# Revit family: Deca_Porta toalha barra 20cm_Acessórios Deca Liv_2040.22.020
name_source: partatom
category: Plumbing Fixtures
units: mm (PartAtom-declared; Revit-internal decimal feet)

## family parameters
Cut with Voids When Loaded = No
Host = Face
Part Type = Normal
Room Calculation Point = No
Round Connector Dimension = Use Diameter
Shared = No

## types (1)
- 2040.C22.020_Cromado
    Acompanha o Produto = Acompanha Parafusos e Buchas para fixação para alvenaria
    Aprovado por = quattroD
    Atendimento ao Cliente = 0800-0117073
    Categoria = ACESSORIOS
    Composição Anel Vedação = -
    Composição Assento = -
    Composição Básica = Liga de Cobre (bronze e latão),Plásticos de Engenharia,Elastômeros
    Composição Componente = -
    Consumo = -
    Cor Interna = -
    Cor Principal = Cromado
    Cor Secundária = -
    Cores Componente = -
    Criado por = quattroD
    Código Pai = 2040.22.020
    Default Elevation = 1100 mm
    Description = Porta toalha barra 20cm
    Informações Complementares = -
    Itens de Instalação = -
    Linha = Acessórios Deca Liv
    Manufacturer = Deca
    Material = Deca_Cromado
    Model = 2040.C22.020
    Norma = Não Possui
    Peso Líquido (Kg) = 0.437
    Pressão máx. funcionamento = -
    Pressão mín. Aquec. Acúmulo = -
    Pressão mín. Aquec. Passagem = -
    Pressão mín. funcionamento = -
    Saída de Esgoto = -
    Segmento = Banheiro Competitivo
    Tipo de dispositivo economizador = -
    Tipo de mecanismo utilizado = -
    Tipo de rosca de entrada = -
    Tipo de rosca de saída = -
    URL = www.deca.com.br
    Vazão na Pressão máx. (L/min) = -
    Vazão na Pressão mín. (L/min) = -

## geometry (parser evidence)
native form markers: Sweep x3
no freeform markers — native parametric forms only
